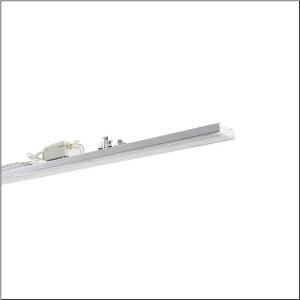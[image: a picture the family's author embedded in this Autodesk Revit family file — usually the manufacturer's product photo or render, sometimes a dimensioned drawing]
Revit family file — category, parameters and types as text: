
# Revit family: licross_r__21_recessed_mo_52tl12dv4fxg3s4_9313
name_source: partatom
category: Lighting Fixtures
units: mm (PartAtom-declared; Revit-internal decimal feet)

## family parameters
Cut with Voids When Loaded = No
Host = Face
Light Source = No
Part Type = Normal
Room Calculation Point = No
Round Connector Dimension = Use Diameter
Shared = No

## types (1)
- --- (1 x LED, 950 lm, 5.5 W, 4000K)
    Apparent Load = 6 VA
    CIE Flux Codes = 72 92 99 100 100
    Color Rendering = 80
    Color Temperature = 4000K
    Default Elevation = 1800 mm
    Description = Licross® 21 Recessed MO, luminaire insert, of sheet steel, galvanised, coil coated, white, length: 2.250mm, width: 66mm, height: 67mm, LED rated luminous flux: 15.420lm, light colour: 840, control gear: DALI 2, with plug, 6-pole, with phase selection, for trunking rail, 9 or 11-core, mains connection: 220..240V, AC, 50/60Hz, rated input power: 89W, for trunking rail, 9-/11-core, halogen-free wiring, for emergency light function, converter,control gear: single battery element, battery: LiFeP04, 9Ah, primary optical cover: cover, of PMMA, light emission: direct distribution, primary light characteristic: symmetric, protection rating (complete): IP40, insulation class (complete): insulation class I (protective earthing), certification: CE, UKCA, protection symbol: D if used in an environment without relevant dust loads with corresponding accessories, impact resistance: IK06, permissible ambient temperature for indoor applications: +5..+35°C, standard: EN 60598-2-22, LABS conformity tested according to VDMA 24364:2018-05, reducing of maximum allowable ambient temperature of 5°C with ceiling mounting, corresponds to IFS (International Featured Standards) requirements for safety and quality in the food industry, packaging unit: 1 piece
    Height = 58 mm
    Lamp = 1 x LED
    Lamp Light Flux = 950 lm
    Lamp Power = 5.5 W
    Lamp count = 1
    Length = 2250 mm
    Luminous efficacy = 173 lm/W
    Manufacturer = Siteco
    ModVariant = No
    Model = 52TL12DV4FXG3S4
    Mounting Place = Ceiling
    Mounting Type = Pendant
    Number of Poles = 1
    OnlyDefault = Yes
    Power Factor = 1
    Product Name = Licross® 21 Recessed MO
    Product group = luminaire insert
    ProductGroupID = 901
    Protection Class = Protection class I
    Protection Degree = IP 40
    RLX_Detail_Level = 1
    RLX_Emergency_Light_Flux = 0 lm
    RLX_Emergency_Type = 0
    RLX_Emergency_Type_DB = No
    RlxData = <blob elided: 30057 chars, md5=66de4097>
    Socket = socket
    Standby Power = 0 W
    System Light Flux = 950 lm
    System Power = 6 W
    Type Comments = : emergency light operation: 3 h
    Type Image = l_1296930.jpg
    URL = http://relux.com
    VarID = @adj_040191
    Voltage = 0 V
    Weight = 0.00 kg
    Width = 66 mm

## geometry (parser evidence)
native form markers: Blend x4, Sweep x10
no freeform markers — native parametric forms only
